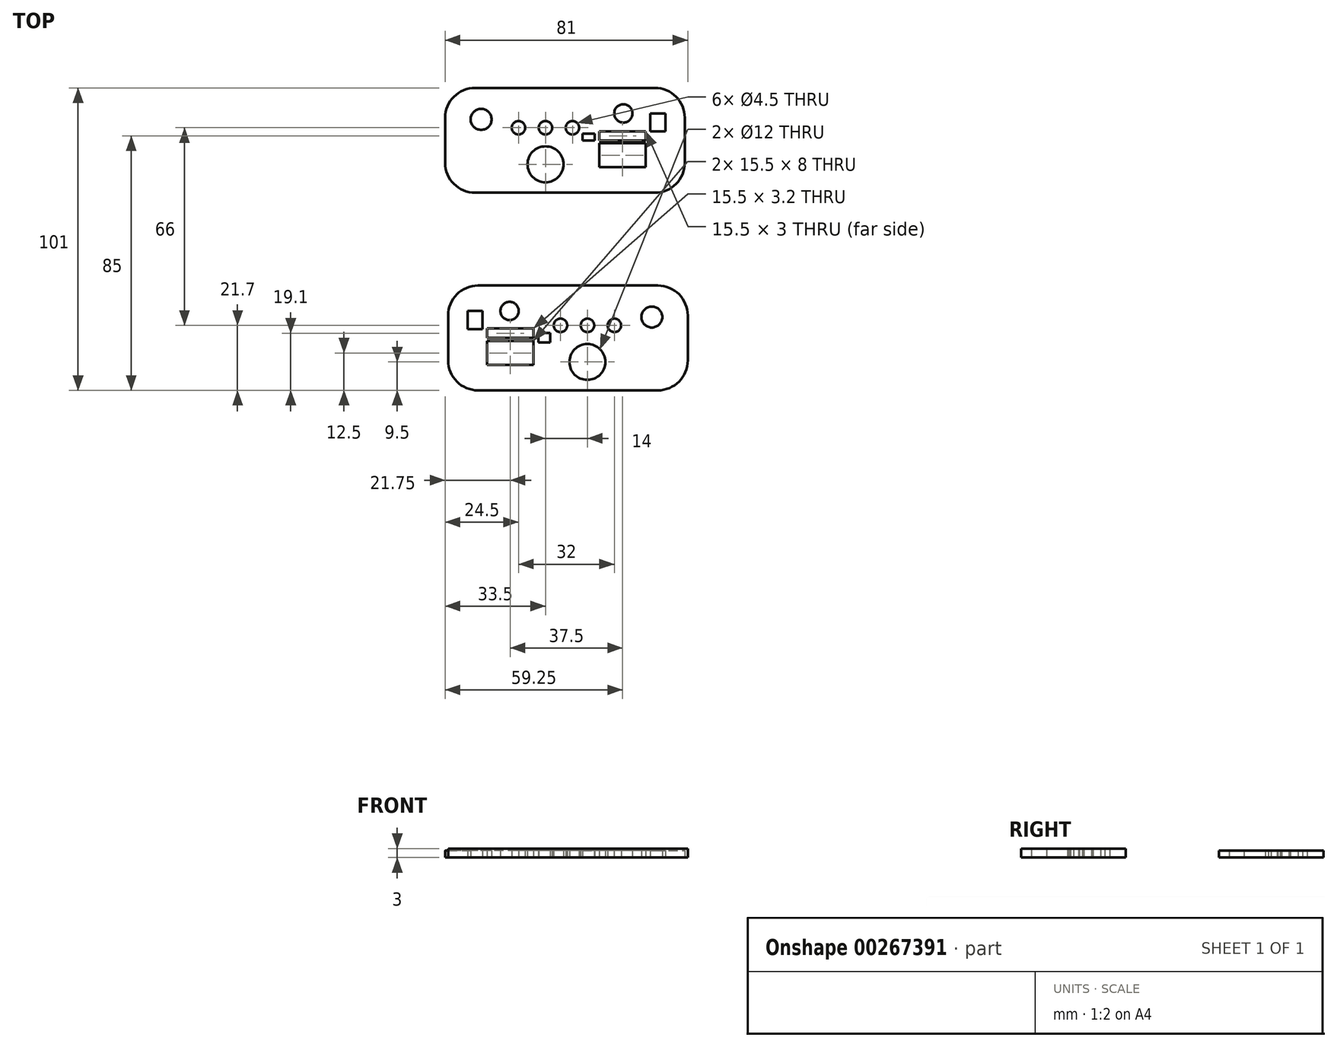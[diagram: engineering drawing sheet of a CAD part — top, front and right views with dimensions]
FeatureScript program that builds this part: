
annotation { "Feature Type Name" : "Feature", "Feature Type Description" : "" }
export const myFeature = defineFeature(function(context is Context, id is Id, definition is map)
    precondition{}
    {
        {
            var Q0;
            Q0=qCreatedBy(makeId("Top.planeOp"),FACE);
            var sketch = newSketch(context, id + "F0", { "sketchPlane" : qUnion([Q0])});
            skLineSegment(sketch, "E0.bottom", {"start": v(43, 83.5) * mm, "end": v(-37, 83.5) * mm});
            skLineSegment(sketch, "E0.top", {"start": v(43, 48.5) * mm, "end": v(-37, 48.5) * mm});
            skLineSegment(sketch, "E0.left", {"start": v(43, 83.5) * mm, "end": v(43, 48.5) * mm});
            skLineSegment(sketch, "E0.right", {"start": v(-37, 83.5) * mm, "end": v(-37, 48.5) * mm});
            skPoint(sketch, "E0.middle", {"position": v(3, 66) * mm});
            skLineSegment(sketch, "E1.bottom", {"start": v(36.5, 81) * mm, "end": v(-30.5, 81) * mm, "construction": true});
            skLineSegment(sketch, "E1.top", {"start": v(36.5, 51) * mm, "end": v(-30.5, 51) * mm, "construction": true});
            skLineSegment(sketch, "E1.left", {"start": v(36.5, 81) * mm, "end": v(36.5, 51) * mm, "construction": true});
            skLineSegment(sketch, "E1.right", {"start": v(-30.5, 81) * mm, "end": v(-30.5, 51) * mm, "construction": true});
            skLineSegment(sketch, "E2", {"start": v(-30.5, 66) * mm, "end": v(-25, 66) * mm, "construction": true});
            skPoint(sketch, "E3", {"position": v(-25, 66) * mm});
            skLineSegment(sketch, "E4", {"start": v(-30.5, 66) * mm, "end": v(-12.5, 66) * mm, "construction": true});
            skLineSegment(sketch, "E5", {"start": v(-30.5, 66) * mm, "end": v(-3.5, 66) * mm, "construction": true});
            skLineSegment(sketch, "E6", {"start": v(-30.5, 66) * mm, "end": v(5.5, 66) * mm, "construction": true});
            skLineSegment(sketch, "E7", {"start": v(36.5, 66) * mm, "end": v(31.5, 66) * mm, "construction": true});
            skLineSegment(sketch, "E8", {"start": v(36.5, 66) * mm, "end": v(30, 66) * mm, "construction": true});
            skLineSegment(sketch, "E9", {"start": v(36.5, 66) * mm, "end": v(14.5, 66) * mm, "construction": true});
            skPoint(sketch, "E10", {"position": v(-12.5, 66) * mm});
            skPoint(sketch, "E11", {"position": v(-3.5, 66) * mm});
            skPoint(sketch, "E12", {"position": v(5.5, 66) * mm});
            skPoint(sketch, "E13", {"position": v(14.5, 66) * mm});
            skPoint(sketch, "E14", {"position": v(30, 66) * mm});
            skPoint(sketch, "E15", {"position": v(31.5, 66) * mm});
            skLineSegment(sketch, "E16", {"start": v(-30.5, 66) * mm, "end": v(-30.5, 70.2) * mm, "construction": true});
            skLineSegment(sketch, "E17", {"start": v(-30.5, 66) * mm, "end": v(-30.5, 73) * mm, "construction": true});
            skLineSegment(sketch, "E18", {"start": v(36.5, 66) * mm, "end": v(36.5, 69) * mm, "construction": true});
            skPoint(sketch, "E19", {"position": v(36.5, 69) * mm});
            skPoint(sketch, "E20", {"position": v(-30.5, 70.2) * mm});
            skPoint(sketch, "E21", {"position": v(-30.5, 73) * mm});
            skLineSegment(sketch, "E22", {"start": v(36.5, 66) * mm, "end": v(36.5, 75) * mm, "construction": true});
            skLineSegment(sketch, "E23", {"start": v(36.5, 66) * mm, "end": v(36.5, 65) * mm, "construction": true});
            skLineSegment(sketch, "E24", {"start": v(36.5, 66) * mm, "end": v(36.5, 57) * mm, "construction": true});
            skPoint(sketch, "E25", {"position": v(36.5, 57) * mm});
            skPoint(sketch, "E26", {"position": v(36.5, 65) * mm});
            skPoint(sketch, "E27", {"position": v(36.5, 75) * mm});
            skCircle(sketch, "E28", {"center": v(-25, 73) * mm, "radius": 3.5 * mm});
            skCircle(sketch, "E29", {"center": v(-12.5, 70.2) * mm, "radius": 2.25 * mm});
            skCircle(sketch, "E30", {"center": v(-3.5, 70.2) * mm, "radius": 2.25 * mm});
            skCircle(sketch, "E31", {"center": v(5.5, 70.2) * mm, "radius": 2.25 * mm});
            skLineSegment(sketch, "E32.bottom", {"start": v(31.5, 75) * mm, "end": v(36.5, 75) * mm});
            skLineSegment(sketch, "E32.top", {"start": v(31.5, 69) * mm, "end": v(36.5, 69) * mm});
            skLineSegment(sketch, "E32.left", {"start": v(31.5, 75) * mm, "end": v(31.5, 69) * mm});
            skLineSegment(sketch, "E32.right", {"start": v(36.5, 75) * mm, "end": v(36.5, 69) * mm});
            skLineSegment(sketch, "E33.bottom", {"start": v(30, 69) * mm, "end": v(14.5, 69) * mm});
            skLineSegment(sketch, "E33.top", {"start": v(30, 66) * mm, "end": v(14.5, 66) * mm});
            skLineSegment(sketch, "E33.left", {"start": v(30, 69) * mm, "end": v(30, 66) * mm});
            skLineSegment(sketch, "E33.right", {"start": v(14.5, 69) * mm, "end": v(14.5, 66) * mm});
            skLineSegment(sketch, "E34.bottom", {"start": v(30, 57) * mm, "end": v(14.5, 57) * mm});
            skLineSegment(sketch, "E34.top", {"start": v(30, 65) * mm, "end": v(14.5, 65) * mm});
            skLineSegment(sketch, "E34.left", {"start": v(30, 57) * mm, "end": v(30, 65) * mm});
            skLineSegment(sketch, "E34.right", {"start": v(14.5, 57) * mm, "end": v(14.5, 65) * mm});
            skLineSegment(sketch, "E35", {"start": v(36.5, 66) * mm, "end": v(22.5, 66) * mm, "construction": true});
            skPoint(sketch, "E36", {"position": v(22.5, 66) * mm});
            skCircle(sketch, "E37", {"center": v(22.5, 75) * mm, "radius": 3.05 * mm});
            skLineSegment(sketch, "E38", {"start": v(5.5, 66) * mm, "end": v(11, 66) * mm, "construction": true});
            skPoint(sketch, "E39", {"position": v(11, 66) * mm});
            skLineSegment(sketch, "E40.bottom", {"start": v(8.87, 66) * mm, "end": v(12.87, 66) * mm});
            skLineSegment(sketch, "E40.top", {"start": v(8.87, 68.2) * mm, "end": v(12.87, 68.2) * mm});
            skLineSegment(sketch, "E40.left", {"start": v(8.87, 66) * mm, "end": v(8.87, 68.2) * mm});
            skLineSegment(sketch, "E40.right", {"start": v(12.87, 66) * mm, "end": v(12.87, 68.2) * mm});
            skCircle(sketch, "E41", {"center": v(-3.5, 58) * mm, "radius": 6 * mm});
            skLineSegment(sketch, "E42", {"start": v(0, 0) * mm, "end": v(62.6, 0) * mm, "construction": true});
            skLineSegment(sketch, "E43", {"start": v(62.6, 0) * mm, "end": v(62.6, 25.57) * mm, "construction": true});
            skLineSegment(sketch, "E44.MirrorCS", {"start": v(-29.5, 0) * mm, "end": v(-29.5, 3) * mm, "construction": true});
            skLineSegment(sketch, "E45.MirrorCS", {"start": v(-29.5, 0) * mm, "end": v(-29.5, -1) * mm, "construction": true});
            skLineSegment(sketch, "E46.MirrorCS", {"start": v(-23, 3.2) * mm, "end": v(-23, 0) * mm});
            skLineSegment(sketch, "E47.MirrorCS", {"start": v(-29.5, 9) * mm, "end": v(-29.5, 3) * mm});
            skLineSegment(sketch, "E48.MirrorCS", {"start": v(1.5, 0) * mm, "end": v(-4, 0) * mm, "construction": true});
            skLineSegment(sketch, "E49.MirrorCS", {"start": v(-5.87, -1.5) * mm, "end": v(-5.87, 1.7) * mm});
            skLineSegment(sketch, "E50.MirrorCS", {"start": v(-29.5, 0) * mm, "end": v(-24.5, 0) * mm, "construction": true});
            skLineSegment(sketch, "E51.MirrorCS", {"start": v(-29.5, 0) * mm, "end": v(-23, 0) * mm, "construction": true});
            skLineSegment(sketch, "E52.MirrorCS", {"start": v(-1.87, -1.5) * mm, "end": v(-1.87, 1.7) * mm});
            skLineSegment(sketch, "E53.MirrorCS", {"start": v(-29.5, 0) * mm, "end": v(-29.5, 9) * mm, "construction": true});
            skLineSegment(sketch, "E54.MirrorCS", {"start": v(-1.87, 1.7) * mm, "end": v(-5.87, 1.7) * mm});
            skLineSegment(sketch, "E55.MirrorCS", {"start": v(-1.87, -1.5) * mm, "end": v(-5.87, -1.5) * mm});
            skLineSegment(sketch, "E56.MirrorCS", {"start": v(-7.5, 3.2) * mm, "end": v(-7.5, 0) * mm});
            skLineSegment(sketch, "E57.MirrorCS", {"start": v(-24.5, 3) * mm, "end": v(-29.5, 3) * mm});
            skLineSegment(sketch, "E58.MirrorCS", {"start": v(-24.5, 9) * mm, "end": v(-29.5, 9) * mm});
            skLineSegment(sketch, "E59.MirrorCS", {"start": v(-24.5, 9) * mm, "end": v(-24.5, 3) * mm});
            skCircle(sketch, "E60.MirrorC", {"center": v(19.5, 4.2) * mm, "radius": 2.25 * mm});
            skLineSegment(sketch, "E61.MirrorCS", {"start": v(-23, 0) * mm, "end": v(-7.5, 0) * mm});
            skLineSegment(sketch, "E62.MirrorCS", {"start": v(37.5, 0) * mm, "end": v(37.5, 7) * mm, "construction": true});
            skCircle(sketch, "E63.MirrorC", {"center": v(10.5, 4.2) * mm, "radius": 2.25 * mm});
            skLineSegment(sketch, "E64.MirrorCS", {"start": v(37.5, 0) * mm, "end": v(19.5, 0) * mm, "construction": true});
            skLineSegment(sketch, "E65.MirrorCS", {"start": v(37.5, 0) * mm, "end": v(32, 0) * mm, "construction": true});
            skLineSegment(sketch, "E66.MirrorCS", {"start": v(-29.5, 15) * mm, "end": v(-29.5, -15) * mm, "construction": true});
            skLineSegment(sketch, "E67.MirrorCS", {"start": v(37.5, 0) * mm, "end": v(37.5, 4.2) * mm, "construction": true});
            skLineSegment(sketch, "E68.MirrorCS", {"start": v(-29.5, 0) * mm, "end": v(-15.5, 0) * mm, "construction": true});
            skCircle(sketch, "E69.MirrorC", {"center": v(32, 7) * mm, "radius": 3.5 * mm});
            skCircle(sketch, "E70.MirrorC", {"center": v(1.5, 4.2) * mm, "radius": 2.25 * mm});
            skPoint(sketch, "E71.MirrorP", {"position": v(-4, 0) * mm});
            skLineSegment(sketch, "E72.MirrorCS", {"start": v(-23, 3.2) * mm, "end": v(-7.5, 3.2) * mm});
            skLineSegment(sketch, "E73.MirrorCS", {"start": v(-29.5, 0) * mm, "end": v(-29.5, -9) * mm, "construction": true});
            skLineSegment(sketch, "E74.MirrorCS", {"start": v(37.5, 0) * mm, "end": v(10.5, 0) * mm, "construction": true});
            skLineSegment(sketch, "E75.MirrorCS", {"start": v(-29.5, 0) * mm, "end": v(-7.5, 0) * mm, "construction": true});
            skPoint(sketch, "E76.MirrorP", {"position": v(-24.5, 0) * mm});
            skPoint(sketch, "E77.MirrorP", {"position": v(4, 0) * mm});
            skLineSegment(sketch, "E78.MirrorCS", {"start": v(-23, -1) * mm, "end": v(-7.5, -1) * mm});
            skPoint(sketch, "E79.MirrorP", {"position": v(-23, 0) * mm});
            skCircle(sketch, "E80.MirrorC", {"center": v(-15.5, 9) * mm, "radius": 3.05 * mm});
            skPoint(sketch, "E81.MirrorP", {"position": v(10.5, 0) * mm});
            skPoint(sketch, "E82.MirrorP", {"position": v(-29.5, -1) * mm});
            skLineSegment(sketch, "E83.MirrorCS", {"start": v(-23, -9) * mm, "end": v(-7.5, -9) * mm});
            skPoint(sketch, "E84.MirrorP", {"position": v(-7.5, 0) * mm});
            skPoint(sketch, "E85.MirrorP", {"position": v(37.5, 4.2) * mm});
            skCircle(sketch, "E86.MirrorC", {"center": v(10.5, -8) * mm, "radius": 6 * mm});
            skPoint(sketch, "E87.MirrorP", {"position": v(19.5, 0) * mm});
            skPoint(sketch, "E88.MirrorP", {"position": v(-29.5, -9) * mm});
            skPoint(sketch, "E89.MirrorP", {"position": v(-15.5, 0) * mm});
            skPoint(sketch, "E90.MirrorP", {"position": v(1.5, 0) * mm});
            skLineSegment(sketch, "E91.MirrorCS", {"start": v(-7.5, -9) * mm, "end": v(-7.5, -1) * mm});
            skPoint(sketch, "E92.MirrorP", {"position": v(-29.5, 3) * mm});
            skPoint(sketch, "E93.MirrorP", {"position": v(-29.5, 9) * mm});
            skLineSegment(sketch, "E94.MirrorCS", {"start": v(37.5, 0) * mm, "end": v(1.5, 0) * mm, "construction": true});
            skLineSegment(sketch, "E95.MirrorCS", {"start": v(37.5, 15) * mm, "end": v(37.5, -15) * mm, "construction": true});
            skLineSegment(sketch, "E96.MirrorCS", {"start": v(-29.5, 15) * mm, "end": v(37.5, 15) * mm, "construction": true});
            skLineSegment(sketch, "E97.MirrorCS", {"start": v(-29.5, -15) * mm, "end": v(37.5, -15) * mm, "construction": true});
            skLineSegment(sketch, "E98.MirrorCS", {"start": v(44, 17.5) * mm, "end": v(44, -17.5) * mm});
            skPoint(sketch, "E99.MirrorP", {"position": v(32, 0) * mm});
            skPoint(sketch, "E100.MirrorP", {"position": v(37.5, 7) * mm});
            skLineSegment(sketch, "E101.MirrorCS", {"start": v(-36, 17.5) * mm, "end": v(-36, -17.5) * mm});
            skLineSegment(sketch, "E102.MirrorCS", {"start": v(-36, -17.5) * mm, "end": v(44, -17.5) * mm});
            skLineSegment(sketch, "E103.MirrorCS", {"start": v(-36, 17.5) * mm, "end": v(44, 17.5) * mm});
            skLineSegment(sketch, "E104.MirrorCS", {"start": v(-23, -9) * mm, "end": v(-23, -1) * mm});
            skSolve(sketch);
        }
        {
            var Q0;
            Q0=makeQuery(id+"F0.imprint","IMPRINT",FACE,{"disambiguationData":[TD([[makeQuery(id+"F0.imprint","IMPRINT",EDGE,{"derivedFrom":sQuery(id+"F0.wireOp",EDGE,"E0.bottom")}),1.0]])]});
            extrude(context, id + "F1", {"entities" : qUnion([Q0]), "depth" : 2.3 * mm});
        }
        {
            var Q0;
            Q0=makeQuery(id+"F1.opExtrude","SWEPT_EDGE",EDGE,{"disambiguationData":[OSD([sQuery(id+"F0.wireOp",EDGE,"E0.bottom"),sQuery(id+"F0.wireOp",EDGE,"E0.left")])]});
            var Q1;
            Q1=makeQuery(id+"F1.opExtrude","SWEPT_EDGE",EDGE,{"disambiguationData":[OSD([sQuery(id+"F0.wireOp",EDGE,"E0.top"),sQuery(id+"F0.wireOp",EDGE,"E0.left")])]});
            var Q2;
            Q2=makeQuery(id+"F1.opExtrude","SWEPT_EDGE",EDGE,{"disambiguationData":[OSD([sQuery(id+"F0.wireOp",EDGE,"E0.top"),sQuery(id+"F0.wireOp",EDGE,"E0.right")])]});
            var Q3;
            Q3=makeQuery(id+"F1.opExtrude","SWEPT_EDGE",EDGE,{"disambiguationData":[OSD([sQuery(id+"F0.wireOp",EDGE,"E0.bottom"),sQuery(id+"F0.wireOp",EDGE,"E0.right")])]});
            fillet(context, id + "F2", {"entities" : qUnion([Q0, Q1, Q2, Q3]), "radius" : 10 * mm, "tangentPropagation" : true, "allowEdgeOverflow" : false});
        }
        {
            var Q0;
            Q0=makeQuery(id+"F0.imprint","IMPRINT",FACE,{"disambiguationData":[TD([[makeQuery(id+"F0.imprint","IMPRINT",EDGE,{"derivedFrom":sQuery(id+"F0.wireOp",EDGE,"E46.MirrorCS")}),-1.0]])]});
            extrude(context, id + "F3", {"entities" : qUnion([Q0]), "depth" : 3 * mm});
        }
        {
            var Q0;
            Q0=makeQuery(id+"F3.opExtrude","SWEPT_EDGE",EDGE,{"disambiguationData":[OSD([sQuery(id+"F0.wireOp",EDGE,"E101.MirrorCS"),sQuery(id+"F0.wireOp",EDGE,"E103.MirrorCS")])]});
            var Q1;
            Q1=makeQuery(id+"F3.opExtrude","SWEPT_EDGE",EDGE,{"disambiguationData":[OSD([sQuery(id+"F0.wireOp",EDGE,"E101.MirrorCS"),sQuery(id+"F0.wireOp",EDGE,"E102.MirrorCS")])]});
            var Q2;
            Q2=makeQuery(id+"F3.opExtrude","SWEPT_EDGE",EDGE,{"disambiguationData":[OSD([sQuery(id+"F0.wireOp",EDGE,"E98.MirrorCS"),sQuery(id+"F0.wireOp",EDGE,"E103.MirrorCS")])]});
            var Q3;
            Q3=makeQuery(id+"F3.opExtrude","SWEPT_EDGE",EDGE,{"disambiguationData":[OSD([sQuery(id+"F0.wireOp",EDGE,"E98.MirrorCS"),sQuery(id+"F0.wireOp",EDGE,"E102.MirrorCS")])]});
            fillet(context, id + "F4", {"entities" : qUnion([Q0, Q1, Q2, Q3]), "radius" : 10 * mm, "tangentPropagation" : true, "allowEdgeOverflow" : false});
        }
    });
